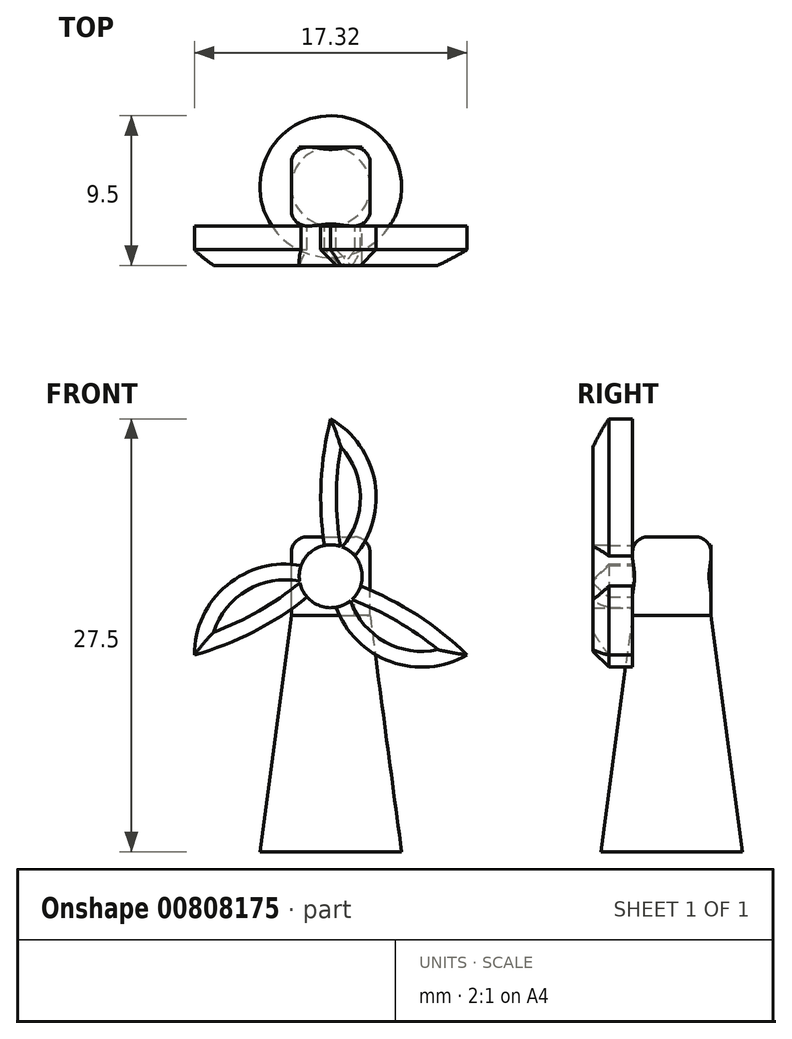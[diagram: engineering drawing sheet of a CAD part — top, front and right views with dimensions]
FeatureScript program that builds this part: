
annotation { "Feature Type Name" : "Feature", "Feature Type Description" : "" }
export const myFeature = defineFeature(function(context is Context, id is Id, definition is map)
    precondition{}
    {
        {
            var Q0;
            Q0=qCreatedBy(makeId("Front.planeOp"),FACE);
            var sketch = newSketch(context, id + "F0", { "sketchPlane" : qUnion([Q0])});
            skLineSegment(sketch, "E0.bottom", {"start": v(-2.5, 15) * mm, "end": v(2.5, 15) * mm});
            skLineSegment(sketch, "E0.top", {"start": v(-2.5, 0) * mm, "end": v(2.5, 0) * mm});
            skLineSegment(sketch, "E0.left", {"start": v(-2.5, 15) * mm, "end": v(-2.5, 0) * mm});
            skLineSegment(sketch, "E0.right", {"start": v(2.5, 15) * mm, "end": v(2.5, 0) * mm});
            skLineSegment(sketch, "E1", {"start": v(-2.5, 15) * mm, "end": v(-4.5, 0) * mm});
            skLineSegment(sketch, "E2", {"start": v(-4.5, 0) * mm, "end": v(-2.5, 0) * mm});
            skLineSegment(sketch, "E3", {"start": v(2.5, 0) * mm, "end": v(4.5, 0) * mm});
            skLineSegment(sketch, "E4", {"start": v(4.5, 0) * mm, "end": v(2.5, 15) * mm});
            skLineSegment(sketch, "E5.top", {"start": v(-2.5, 20) * mm, "end": v(2.5, 20) * mm});
            skLineSegment(sketch, "E5.left", {"start": v(-2.5, 15) * mm, "end": v(-2.5, 20) * mm});
            skLineSegment(sketch, "E5.right", {"start": v(2.5, 15) * mm, "end": v(2.5, 20) * mm});
            skPoint(sketch, "E6", {"position": v(0, 17.5) * mm});
            skCircle(sketch, "E7", {"center": v(0, 17.5) * mm, "radius": 2 * mm});
            skLineSegment(sketch, "E8", {"start": v(0, 20) * mm, "end": v(0, 0) * mm});
            skSolve(sketch);
        }
        {
            var Q0;
            {var subQ0=sQuery(id+"F0.wireOp",EDGE,"E0.left");Q0=makeQuery(id+"F0.imprint","IMPRINT",FACE,{"disambiguationData":[TD([[makeQuery(id+"F0.imprint","IMPRINT",EDGE,{"derivedFrom":subQ0}),1.0]])]});}
            var Q1;
            Q1=makeQuery(id+"F0.imprint","IMPRINT",FACE,{"disambiguationData":[TD([[makeQuery(id+"F0.imprint","IMPRINT",EDGE,{"derivedFrom":sQuery(id+"F0.wireOp",EDGE,"E0.left")}),-1.0]])]});
            var Q2;
            Q2=sQuery(id+"F0.wireOp",EDGE,"E8");
            revolve(context, id + "F1", {"surfaceOperationType" : NewSurfaceOperationType.NEW, "entities" : qUnion([Q0, Q1]), "axis" : qUnion([Q2]), "revolveType" : RevolveType.FULL});
        }
        {
            var Q0;
            {var subQ4=sQuery(id+"F0.wireOp",EDGE,"E5.right");Q0=makeQuery(id+"F0.imprint","IMPRINT",FACE,{"disambiguationData":[TD([[makeQuery(id+"F0.imprint","IMPRINT",EDGE,{"derivedFrom":subQ4}),1.0]])]});}
            var Q1;
            {var subQ4=sQuery(id+"F0.wireOp",EDGE,"E5.left");Q1=makeQuery(id+"F0.imprint","IMPRINT",FACE,{"disambiguationData":[TD([[makeQuery(id+"F0.imprint","IMPRINT",EDGE,{"derivedFrom":subQ4}),-1.0]])]});}
            extrude(context, id + "F2", {"entities" : qUnion([Q0, Q1]), "operationType" : NewBodyOperationType.ADD, "endBound" : BoundingType.SYMMETRIC, "depth" : 5 * mm, "offsetDistance" : 25 * mm});
        }
        {
            var Q0;
            Q0=makeQuery(id+"F2.opExtrude","CAP_EDGE",EDGE,{"disambiguationData":[OSD([sQuery(id+"F0.wireOp",EDGE,"E5.right")])],"isStart":false});
            var Q1;
            Q1=makeQuery(id+"F2.opExtrude","CAP_EDGE",EDGE,{"disambiguationData":[OSD([sQuery(id+"F0.wireOp",EDGE,"E5.right")])],"isStart":true});
            var Q2;
            Q2=makeQuery(id+"F2.opExtrude","CAP_EDGE",EDGE,{"disambiguationData":[OSD([sQuery(id+"F0.wireOp",EDGE,"E5.left")])],"isStart":true});
            var Q3;
            Q3=makeQuery(id+"F2.opExtrude","SWEPT_EDGE",EDGE,{"disambiguationData":[OSD([sQuery(id+"F0.wireOp",EDGE,"E5.top"),sQuery(id+"F0.wireOp",EDGE,"E5.left")])]});
            var Q4;
            Q4=makeQuery(id+"F2.opExtrude","CAP_EDGE",EDGE,{"disambiguationData":[OSD([sQuery(id+"F0.wireOp",EDGE,"E5.top")])],"isStart":true});
            var Q5;
            Q5=makeQuery(id+"F2.opExtrude","CAP_EDGE",EDGE,{"disambiguationData":[OSD([sQuery(id+"F0.wireOp",EDGE,"E5.top")])],"isStart":false});
            var Q6;
            Q6=makeQuery(id+"F2.opExtrude","CAP_EDGE",EDGE,{"disambiguationData":[OSD([sQuery(id+"F0.wireOp",EDGE,"E5.left")])],"isStart":false});
            var Q7;
            Q7=makeQuery(id+"F2.opExtrude","SWEPT_EDGE",EDGE,{"disambiguationData":[OSD([sQuery(id+"F0.wireOp",EDGE,"E5.top"),sQuery(id+"F0.wireOp",EDGE,"E5.right")])]});
            fillet(context, id + "F3", {"entities" : qUnion([Q0, Q1, Q2, Q3, Q4, Q5, Q6, Q7]), "radius" : 1 * mm, "tangentPropagation" : true, "allowEdgeOverflow" : false});
        }
        {
            var Q0;
            {var subQ0=sQuery(id+"F0.wireOp",EDGE,"E8");var subQ1=sQuery(id+"F0.wireOp",EDGE,"E7");var subQ2=makeQuery(id+"F0.imprint","INTERSECT",VERTEX,{"disambiguationData":[OD(0.0)],"derivedFrom":[subQ1,subQ0]});Q0=makeQuery(id+"F0.imprint","IMPRINT",FACE,{"disambiguationData":[TD([[makeQuery(id+"F0.imprint","IMPRINT",EDGE,{"disambiguationData":[TD([[subQ2,1.0]])],"derivedFrom":subQ1}),1.0]])]});}
            var Q1;
            {var subQ0=sQuery(id+"F0.wireOp",EDGE,"E8");var subQ1=sQuery(id+"F0.wireOp",EDGE,"E7");var subQ2=makeQuery(id+"F0.imprint","INTERSECT",VERTEX,{"disambiguationData":[OD(0.0)],"derivedFrom":[subQ1,subQ0]});Q1=makeQuery(id+"F0.imprint","IMPRINT",FACE,{"disambiguationData":[TD([[makeQuery(id+"F0.imprint","IMPRINT",EDGE,{"disambiguationData":[TD([[subQ2,-1.0]])],"derivedFrom":subQ1}),1.0]])]});}
            extrude(context, id + "F4", {"entities" : qUnion([Q0, Q1]), "operationType" : NewBodyOperationType.ADD, "depth" : 5 * mm, "offsetDistance" : 25 * mm, "hasSecondDirection" : true, "secondDirectionOppositeDirection" : true, "secondDirectionDepth" : 2.5 * mm});
        }
        {
            var Q0;
            Q0=qCreatedBy(makeId("Front.planeOp"),FACE);
            var sketch = newSketch(context, id + "F5", { "sketchPlane" : qUnion([Q0])});
            skPoint(sketch, "E9", {"position": v(0, 17.5) * mm});
            skCircle(sketch, "E10", {"center": v(0, 17.5) * mm, "radius": 2 * mm});
            skLineSegment(sketch, "E11", {"start": v(0, 17.5) * mm, "end": v(-8.66, 12.5) * mm});
            skLineSegment(sketch, "E12", {"start": v(0, 17.5) * mm, "end": v(8.66, 12.5) * mm});
            skLineSegment(sketch, "E13", {"start": v(0, 17.5) * mm, "end": v(0, 27.5) * mm});
            skArc(sketch, "E14", {"start": v(0, 17.5) * mm, "mid": v(-5.77, 17.5) * mm, "end": v(-8.66, 12.5) * mm});
            skArc(sketch, "E15", {"start": v(-8.66, 12.5) * mm, "mid": v(-4.01, 14.45) * mm, "end": v(0, 17.5) * mm});
            skArc(sketch, "E16", {"start": v(0, 17.5) * mm, "mid": v(2.89, 12.5) * mm, "end": v(8.66, 12.5) * mm});
            skArc(sketch, "E17", {"start": v(8.66, 12.5) * mm, "mid": v(4.65, 15.55) * mm, "end": v(0, 17.5) * mm});
            skArc(sketch, "E18", {"start": v(0, 17.5) * mm, "mid": v(2.89, 22.5) * mm, "end": v(0, 27.5) * mm});
            skArc(sketch, "E19", {"start": v(0, 27.5) * mm, "mid": v(-0.64, 22.5) * mm, "end": v(0, 17.5) * mm});
            skSolve(sketch);
        }
        {
            var Q0;
            {var subQ0=sQuery(id+"F5.wireOp",EDGE,"E14");var subQ1=sQuery(id+"F5.wireOp",EDGE,"E10");var subQ2=makeQuery(id+"F5.imprint","INTERSECT",VERTEX,{"derivedFrom":[subQ1,subQ0]});Q0=makeQuery(id+"F5.imprint","IMPRINT",FACE,{"disambiguationData":[TD([[makeQuery(id+"F5.imprint","IMPRINT",EDGE,{"disambiguationData":[TD([[subQ2,-1.0]])],"derivedFrom":subQ1}),-1.0]])]});}
            var Q1;
            {var subQ0=sQuery(id+"F5.wireOp",EDGE,"E15");var subQ1=sQuery(id+"F5.wireOp",EDGE,"E10");var subQ2=makeQuery(id+"F5.imprint","INTERSECT",VERTEX,{"derivedFrom":[subQ1,subQ0]});Q1=makeQuery(id+"F5.imprint","IMPRINT",FACE,{"disambiguationData":[TD([[makeQuery(id+"F5.imprint","IMPRINT",EDGE,{"disambiguationData":[TD([[subQ2,1.0]])],"derivedFrom":subQ1}),-1.0]])]});}
            var Q2;
            {var subQ0=sQuery(id+"F5.wireOp",EDGE,"E18");var subQ1=sQuery(id+"F5.wireOp",EDGE,"E10");var subQ2=makeQuery(id+"F5.imprint","INTERSECT",VERTEX,{"derivedFrom":[subQ1,subQ0]});Q2=makeQuery(id+"F5.imprint","IMPRINT",FACE,{"disambiguationData":[TD([[makeQuery(id+"F5.imprint","IMPRINT",EDGE,{"disambiguationData":[TD([[subQ2,-1.0]])],"derivedFrom":subQ1}),-1.0]])]});}
            var Q3;
            {var subQ0=sQuery(id+"F5.wireOp",EDGE,"E19");var subQ1=sQuery(id+"F5.wireOp",EDGE,"E10");var subQ2=makeQuery(id+"F5.imprint","INTERSECT",VERTEX,{"derivedFrom":[subQ1,subQ0]});Q3=makeQuery(id+"F5.imprint","IMPRINT",FACE,{"disambiguationData":[TD([[makeQuery(id+"F5.imprint","IMPRINT",EDGE,{"disambiguationData":[TD([[subQ2,1.0]])],"derivedFrom":subQ1}),-1.0]])]});}
            var Q4;
            {var subQ0=sQuery(id+"F5.wireOp",EDGE,"E16");var subQ1=sQuery(id+"F5.wireOp",EDGE,"E10");var subQ2=makeQuery(id+"F5.imprint","INTERSECT",VERTEX,{"derivedFrom":[subQ1,subQ0]});Q4=makeQuery(id+"F5.imprint","IMPRINT",FACE,{"disambiguationData":[TD([[makeQuery(id+"F5.imprint","IMPRINT",EDGE,{"disambiguationData":[TD([[subQ2,-1.0]])],"derivedFrom":subQ1}),-1.0]])]});}
            var Q5;
            {var subQ0=sQuery(id+"F5.wireOp",EDGE,"E17");var subQ1=sQuery(id+"F5.wireOp",EDGE,"E10");var subQ2=makeQuery(id+"F5.imprint","INTERSECT",VERTEX,{"derivedFrom":[subQ1,subQ0]});Q5=makeQuery(id+"F5.imprint","IMPRINT",FACE,{"disambiguationData":[TD([[makeQuery(id+"F5.imprint","IMPRINT",EDGE,{"disambiguationData":[TD([[subQ2,1.0]])],"derivedFrom":subQ1}),-1.0]])]});}
            extrude(context, id + "F6", {"entities" : qUnion([Q0, Q1, Q2, Q3, Q4, Q5]), "operationType" : NewBodyOperationType.ADD, "depth" : 5 * mm, "offsetDistance" : 25 * mm, "hasSecondDirection" : true, "secondDirectionOppositeDirection" : false, "secondDirectionDepth" : 2.5 * mm});
        }
        {
            var Q0;
            Q0=makeQuery(id+"F6.opExtrude","CAP_EDGE",EDGE,{"disambiguationData":[OSD([sQuery(id+"F5.wireOp",EDGE,"E14")])],"isStart":false});
            var Q1;
            Q1=makeQuery(id+"F6.opExtrude","CAP_EDGE",EDGE,{"disambiguationData":[OSD([sQuery(id+"F5.wireOp",EDGE,"E15")])],"isStart":false});
            var Q2;
            Q2=makeQuery(id+"F6.opExtrude","CAP_EDGE",EDGE,{"disambiguationData":[OSD([sQuery(id+"F5.wireOp",EDGE,"E16")])],"isStart":false});
            var Q3;
            Q3=makeQuery(id+"F6.opExtrude","CAP_EDGE",EDGE,{"disambiguationData":[OSD([sQuery(id+"F5.wireOp",EDGE,"E17")])],"isStart":false});
            var Q4;
            Q4=makeQuery(id+"F6.opExtrude","CAP_EDGE",EDGE,{"disambiguationData":[OSD([sQuery(id+"F5.wireOp",EDGE,"E19")])],"isStart":false});
            var Q5;
            Q5=makeQuery(id+"F6.opExtrude","CAP_EDGE",EDGE,{"disambiguationData":[OSD([sQuery(id+"F5.wireOp",EDGE,"E18")])],"isStart":false});
            chamfer(context, id + "F7", {"entities" : qUnion([Q0, Q1, Q2, Q3, Q4, Q5]), "width" : 1 * mm, "tangentPropagation" : true});
        }
    });
